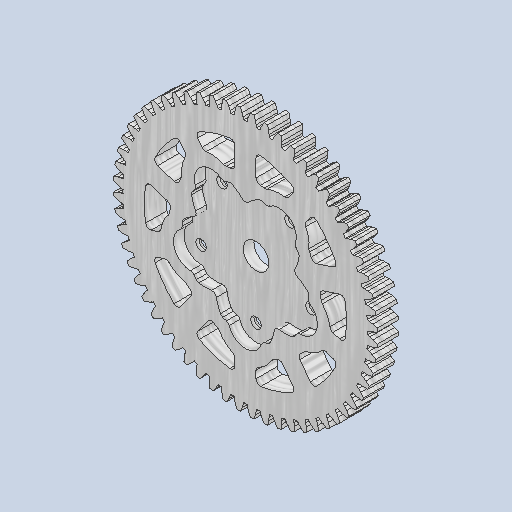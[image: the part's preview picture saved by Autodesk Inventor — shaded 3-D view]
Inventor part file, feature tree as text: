
AUTODESK INVENTOR PART (.ipt)
format: ipt  version: 2023 (Build 270158030, 158C)  size: 1,592,832 bytes
history: native  units: mm
features: extrude x3, sketch x3, fillet x1, chamfer x1, projected_geometry x1
ambient origin geometry x8: Origin, YZ Plane, XZ Plane, XY Plane, X Axis, Y Axis, Z Axis, Center Point
bodies: Solid1 (feature_tree)
feature tree (9):
  extrude  "Extrusion1"  Depth=2.5mm TaperAngle=0.0deg
  extrude  "押し出し2"  Depth=5.0mm
  extrude  "押し出し4"  Depth=5.0mm
  fillet  "フィレット3"  Radius=50.0mm
  chamfer  "面取り1"  [1 undecoded]
  sketch  "Sketch1"  dims[d0=5.0mm d1=0.0mm d6=2.5mm d7=0.0mm d16=5.0mm d17=5.0mm d18=50.0mm d20=360.0deg d22=0.0mm d23=0.0mm d24=3.0mm d25=1.0mm d26=1.75mm d27=2.0mm d28=45.0deg]
  sketch  "スケッチ3"
  sketch  "スケッチ6"
  projected_geometry  "投影ループ3"
note: 1 required parameter value undecoded (feature->parameter linkage not recoverable at this tier; creation-order binding heuristic only, values carry confidence <= 0.55)
